SOLIDWORKS PART (.sldprt)
format: sldprt  version: not decoded by parser v0  size: 157,696 bytes
history: native  units: mm
features: sketch x3, extrude x3, fillet x3, material x1, shell x1 (+13 scaffold rows collapsed)
feature tree (24):
  scaffold x13  (default folders/planes/origin — collapsed)
  material  "Material <not specified>"
  sketch  "Sketch1"  dims[D1=10.0mm D2=10.0mm D3=10.0mm D4=10.0mm]
  extrude  "Boss-Extrude1"  Depth=10mm
  sketch  "Sketch2"  dims[c1.D1=~20.263527mm c1.D4=50.0mm c1.D5=50.0mm c1.D6=25.0mm c2.D1=101.6mm c2.D2=50.8mm c2.D3=~68.550647mm c2.D4=101.6mm c3.D3=75.0mm c3.D6=~1.982255mm]
  extrude  "Boss-Extrude2"  Depth=2mm
  sketch  "Sketch3"  dims[D1=75.0mm D2=101.6mm]
  extrude  "Boss-Extrude3"  Depth=30mm
  fillet  "Fillet1"  Radius=10mm
  fillet  "Fillet2"  Radius=10mm
  fillet  "Fillet3"  Radius=10mm
  shell  "Shell1"  Thickness=2mm
decode coverage: 10 of 10 modeling features carry decoded parameters
note: ~ marks probable driven/reference dimensions
note: suppression state not decoded; provenance and decode notes live in map.json
